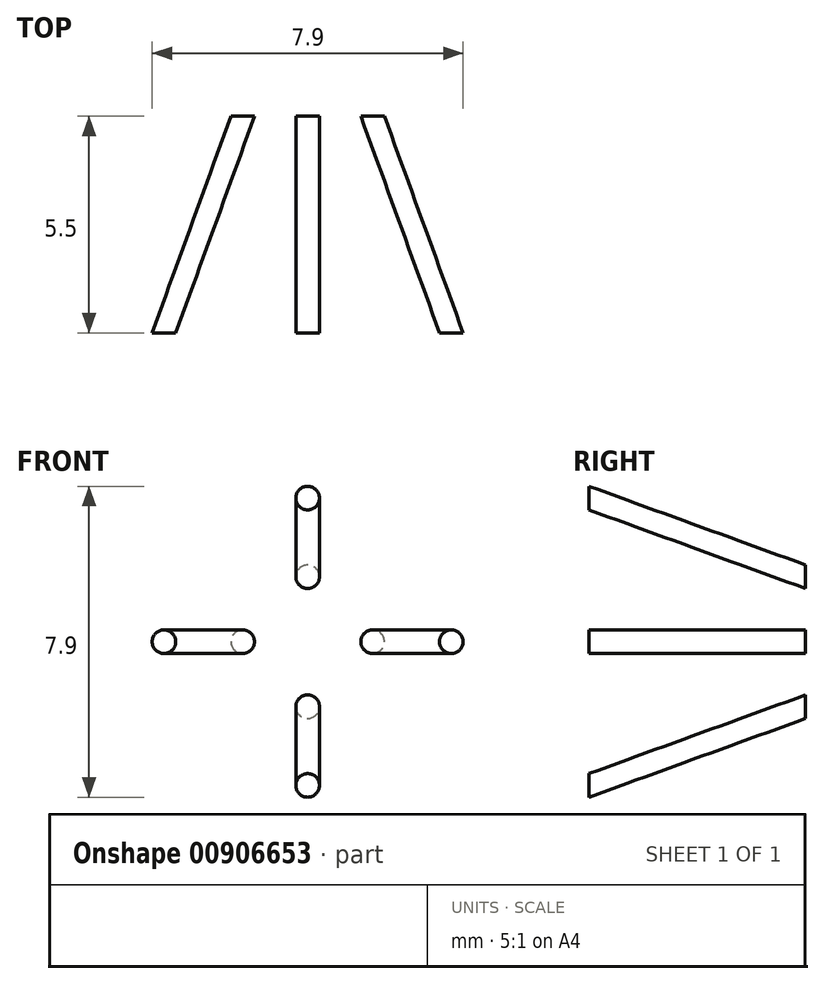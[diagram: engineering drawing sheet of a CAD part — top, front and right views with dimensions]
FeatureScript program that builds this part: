
annotation { "Feature Type Name" : "Feature", "Feature Type Description" : "" }
export const myFeature = defineFeature(function(context is Context, id is Id, definition is map)
    precondition{}
    {
        {
            var Q0;
            Q0=qCreatedBy(makeId("Top.planeOp"),FACE);
            var sketch = newSketch(context, id + "F0", { "sketchPlane" : qUnion([Q0])});
            skLineSegment(sketch, "E0", {"start": v(-1.2, 0) * mm, "end": v(-1.2, 5.5) * mm});
            skLineSegment(sketch, "E1", {"start": v(-1.2, 5.5) * mm, "end": v(-3.2, 0) * mm});
            skLineSegment(sketch, "E2", {"start": v(-3.2, 0) * mm, "end": v(-1.2, 0) * mm});
            skLineSegment(sketch, "E3", {"start": v(-1.2, 5.5) * mm, "end": v(0, 5.5) * mm});
            skLineSegment(sketch, "E4", {"start": v(0, 5.5) * mm, "end": v(0, 0) * mm});
            skLineSegment(sketch, "E5", {"start": v(0, 0) * mm, "end": v(-1.2, 0) * mm});
            skSolve(sketch);
        }
        {
            var Q0;
            Q0=makeQuery(id+"F0.imprint","IMPRINT",FACE,{"disambiguationData":[TD([[makeQuery(id+"F0.imprint","IMPRINT",EDGE,{"derivedFrom":sQuery(id+"F0.wireOp",EDGE,"E0")}),1.0]])]});
            var Q1;
            Q1=sQuery(id+"F0.wireOp",EDGE,"E4");
            revolve(context, id + "F1", {"surfaceOperationType" : NewSurfaceOperationType.NEW, "entities" : qUnion([Q0]), "axis" : qUnion([Q1]), "revolveType" : RevolveType.FULL});
        }
        {
            var Q0;
            Q0=sQuery(id+"F0.wireOp",EDGE,"E0");
            cPoint(context, id + "F2", {"entities" : qUnion([Q0]), "parameter" : 0.5});
        }
        {
            var Q0;
            Q0=qCreatedBy(id+"F2",VERTEX);
            var Q1;
            Q1=makeQuery(id+"F1.opRevolve","SWEPT_EDGE",EDGE,{"disambiguationData":[OSD([sQuery(id+"F0.wireOp",EDGE,"E1"),sQuery(id+"F0.wireOp",EDGE,"E2")])]});
            cPlane(context, id + "F3", {"entities" : qUnion([Q0, Q1]), "cplaneType" : CPlaneType.LINE_ANGLE, "offset" : 25 * mm, "angle" : 0 * degree, "width" : 150 * mm, "height" : 150 * mm});
        }
        {
            var Q0;
            Q0=qCreatedBy(id+"F3.planeOp",FACE);
            var sketch = newSketch(context, id + "F4", { "sketchPlane" : qUnion([Q0])});
            skLineSegment(sketch, "E6", {"start": v(-3.2, 0) * mm, "end": v(-1.2, 5.5) * mm});
            skLineSegment(sketch, "E7", {"start": v(-4.1, 0) * mm, "end": v(-2.1, 5.5) * mm});
            skLineSegment(sketch, "E8", {"start": v(-2.1, 5.5) * mm, "end": v(-1.2, 5.5) * mm});
            skLineSegment(sketch, "E9", {"start": v(-3.2, 0) * mm, "end": v(-4.1, 0) * mm});
            skSolve(sketch);
        }
        {
            var Q0;
            Q0=sQuery(id+"F4.wireOp",EDGE,"E9");
            cPlane(context, id + "F5", {"entities" : qUnion([Q0]), "cplaneType" : CPlaneType.LINE_ANGLE, "offset" : 25 * mm, "angle" : 0 * degree, "width" : 150 * mm, "height" : 150 * mm});
        }
        {
            var Q0;
            Q0=qCreatedBy(id+"F5.planeOp",FACE);
            var sketch = newSketch(context, id + "F6", { "sketchPlane" : qUnion([Q0])});
            skCircle(sketch, "E10", {"center": v(-3.65, 0) * mm, "radius": 0.45 * mm});
            skSolve(sketch);
        }
        {
            var Q0;
            Q0=makeQuery(id+"F6.imprint","IMPRINT",FACE,{"disambiguationData":[TD([[makeQuery(id+"F6.imprint","IMPRINT",EDGE,{"derivedFrom":sQuery(id+"F6.wireOp",EDGE,"E10")}),1.0]])]});
            var Q1;
            Q1=sQuery(id+"F4.wireOp",EDGE,"E6");
            sweep(context, id + "F7", {"profiles" : qUnion([Q0]), "path" : qUnion([Q1])});
        }
        {
            var Q0;
            Q0=makeQuery(id+"F7.opSweep","CAP_FACE",FACE,{"disambiguationData":[OSD([sQuery(id+"F4.wireOp",VERTEX,"E6.start"),sQuery(id+"F6.wireOp",EDGE,"E10")])],"isStart":true});
            var sketch = newSketch(context, id + "F8", { "sketchPlane" : qUnion([Q0])});
            skCircle(sketch, "E11", {"center": v(-3.65, 0) * mm, "radius": 0.3 * mm});
            skSolve(sketch);
        }
        {
            var Q0;
            Q0=makeQuery(id+"F8.imprint","IMPRINT",FACE,{"disambiguationData":[TD([[makeQuery(id+"F8.imprint","IMPRINT",EDGE,{"derivedFrom":sQuery(id+"F8.wireOp",EDGE,"E11")}),1.0]])]});
            var Q1;
            Q1=sQuery(id+"F0.wireOp",EDGE,"E1");
            sweep(context, id + "F9", {"profiles" : qUnion([Q0]), "path" : qUnion([Q1])});
        }
        {
            var Q0;
            Q0=makeQuery(id+"F9.opSweep","SWEPT_BODY",BODY,{"disambiguationData":[OSD([sQuery(id+"F0.wireOp",EDGE,"E1"),sQuery(id+"F8.wireOp",EDGE,"E11")])]});
            var Q1;
            Q1=makeQuery(id+"F7.opSweep","SWEPT_BODY",BODY,{"disambiguationData":[OSD([sQuery(id+"F4.wireOp",EDGE,"E6"),sQuery(id+"F6.wireOp",EDGE,"E10")])]});
            var Q2;
            Q2=makeQuery(id+"F1.opRevolve","SWEPT_EDGE",EDGE,{"disambiguationData":[OSD([sQuery(id+"F0.wireOp",EDGE,"E1"),sQuery(id+"F0.wireOp",EDGE,"E2")])]});
            circularPattern(context, id + "F10", {"entities" : qUnion([Q0, Q1]), "axis" : qUnion([Q2]), "angle" : 360 * degree, "instanceCount" : 4, "equalSpace" : true});
        }
        {
            var Q0;
            Q0=makeQuery(id+"F7.opSweep","SWEPT_BODY",BODY,{"disambiguationData":[OSD([sQuery(id+"F4.wireOp",EDGE,"E6"),sQuery(id+"F6.wireOp",EDGE,"E10")])]});
            deleteBodies(context, id + "F11", {"entities" : qUnion([Q0])});
        }
        {
            var Q0;
            Q0=makeQuery(id+"F10.opPattern","COPY",BODY,{"derivedFrom":makeQuery(id+"F7.opSweep","SWEPT_BODY",BODY,{"disambiguationData":[OSD([sQuery(id+"F4.wireOp",EDGE,"E6"),sQuery(id+"F6.wireOp",EDGE,"E10")])]}),"instanceName":"1"});
            deleteBodies(context, id + "F12", {"entities" : qUnion([Q0])});
        }
        {
            var Q0;
            Q0=makeQuery(id+"F10.opPattern","COPY",BODY,{"derivedFrom":makeQuery(id+"F7.opSweep","SWEPT_BODY",BODY,{"disambiguationData":[OSD([sQuery(id+"F4.wireOp",EDGE,"E6"),sQuery(id+"F6.wireOp",EDGE,"E10")])]}),"instanceName":"2"});
            deleteBodies(context, id + "F13", {"entities" : qUnion([Q0])});
        }
        {
            var Q0;
            Q0=makeQuery(id+"F10.opPattern","COPY",BODY,{"derivedFrom":makeQuery(id+"F7.opSweep","SWEPT_BODY",BODY,{"disambiguationData":[OSD([sQuery(id+"F4.wireOp",EDGE,"E6"),sQuery(id+"F6.wireOp",EDGE,"E10")])]}),"instanceName":"3"});
            deleteBodies(context, id + "F14", {"entities" : qUnion([Q0])});
        }
        {
            var Q0;
            Q0=makeQuery(id+"F1.opRevolve","SWEPT_BODY",BODY,{"disambiguationData":[OSD([sQuery(id+"F0.wireOp",EDGE,"E0"),sQuery(id+"F0.wireOp",EDGE,"E1"),sQuery(id+"F0.wireOp",EDGE,"E2")])]});
            deleteBodies(context, id + "F15", {"entities" : qUnion([Q0])});
        }
    });
